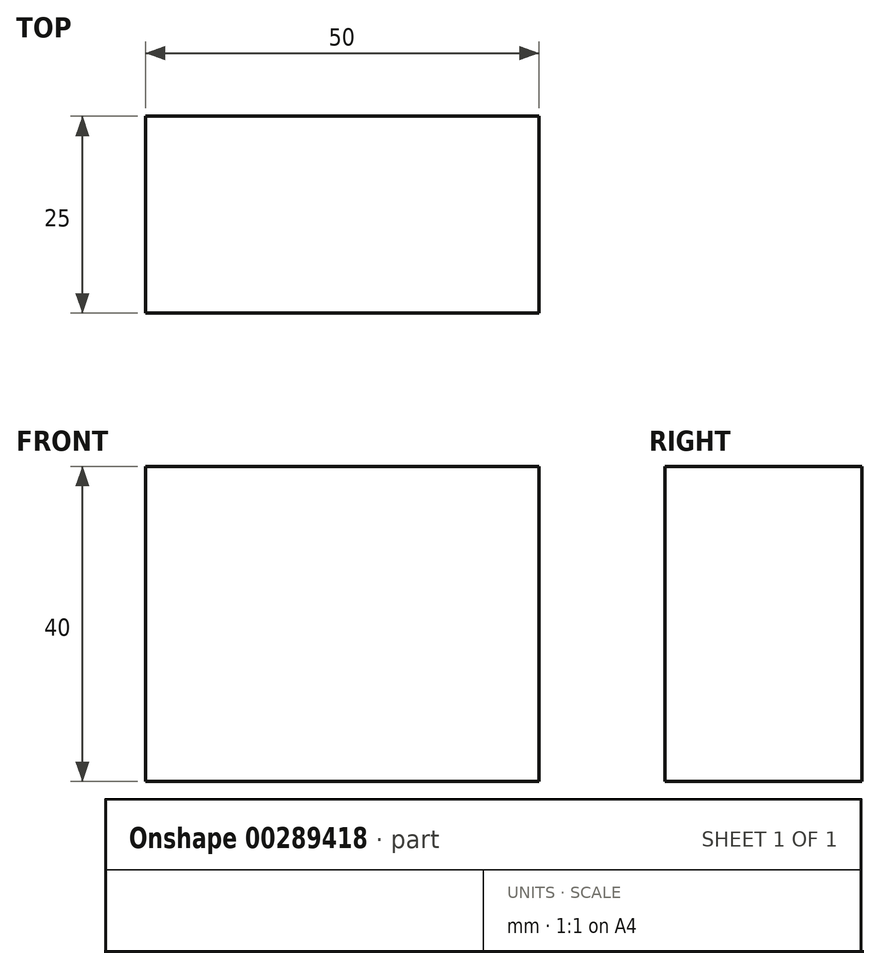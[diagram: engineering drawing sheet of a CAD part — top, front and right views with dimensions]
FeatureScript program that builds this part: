
annotation { "Feature Type Name" : "Feature", "Feature Type Description" : "" }
export const myFeature = defineFeature(function(context is Context, id is Id, definition is map)
    precondition{}
    {
        {
            var Q0;
            Q0=qCreatedBy(makeId("Front.planeOp"),FACE);
            var sketch = newSketch(context, id + "F0", { "sketchPlane" : qUnion([Q0])});
            skLineSegment(sketch, "E0.bottom", {"start": v(0, 0) * mm, "end": v(50, 0) * mm});
            skLineSegment(sketch, "E0.top", {"start": v(0, -40) * mm, "end": v(50, -40) * mm});
            skLineSegment(sketch, "E0.left", {"start": v(0, 0) * mm, "end": v(0, -40) * mm});
            skLineSegment(sketch, "E0.right", {"start": v(50, 0) * mm, "end": v(50, -40) * mm});
            skSolve(sketch);
        }
        {
            var Q0;
            Q0=makeQuery(id+"F0.imprint","IMPRINT",FACE,{"disambiguationData":[TD([[makeQuery(id+"F0.imprint","IMPRINT",EDGE,{"derivedFrom":sQuery(id+"F0.wireOp",EDGE,"E0.bottom")}),-1.0]])]});
            extrude(context, id + "F1", {"entities" : qUnion([Q0]), "depth" : 25 * mm});
        }
    });
